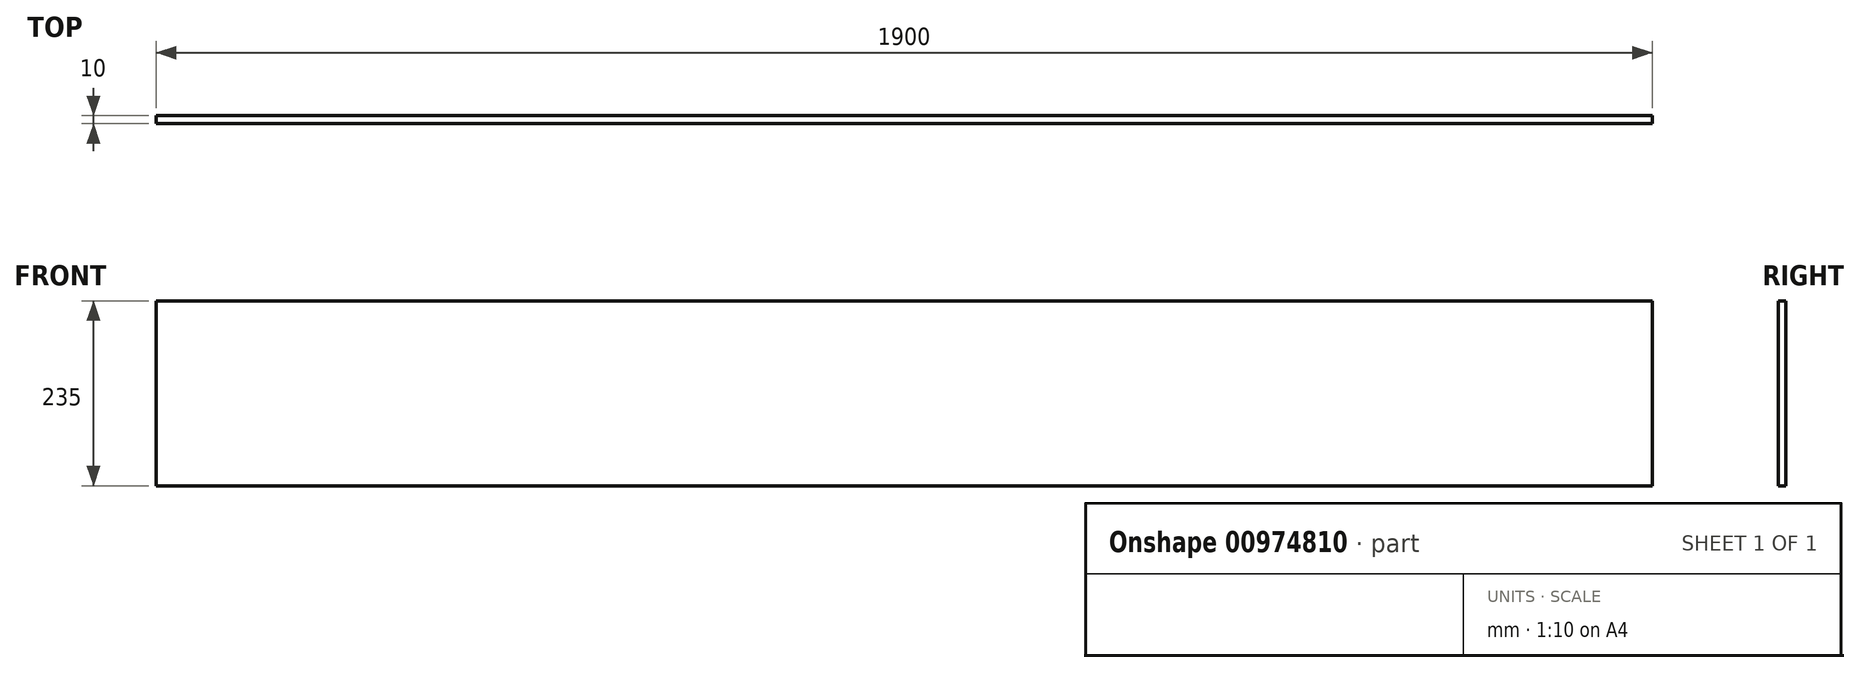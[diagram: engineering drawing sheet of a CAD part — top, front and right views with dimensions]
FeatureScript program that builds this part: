
annotation { "Feature Type Name" : "Feature", "Feature Type Description" : "" }
export const myFeature = defineFeature(function(context is Context, id is Id, definition is map)
    precondition{}
    {
        {
            var Q0;
            Q0=qCreatedBy(makeId("Front.planeOp"),FACE);
            var sketch = newSketch(context, id + "F0", { "sketchPlane" : qUnion([Q0])});
            skLineSegment(sketch, "E0.bottom", {"start": v(-950, -117.5) * mm, "end": v(950, -117.5) * mm});
            skLineSegment(sketch, "E0.top", {"start": v(-950, 117.5) * mm, "end": v(950, 117.5) * mm});
            skLineSegment(sketch, "E0.left", {"start": v(-950, -117.5) * mm, "end": v(-950, 117.5) * mm});
            skLineSegment(sketch, "E0.right", {"start": v(950, -117.5) * mm, "end": v(950, 117.5) * mm});
            skPoint(sketch, "E0.middle", {"position": v(0, 0) * mm});
            skSolve(sketch);
        }
        {
            var Q0;
            Q0 = qSketchRegion(id + "F0", true);
            extrude(context, id + "F1", {"entities" : qUnion([Q0]), "endBound" : BoundingType.SYMMETRIC, "depth" : 10 * mm, "offsetDistance" : 25 * mm});
        }
    });
